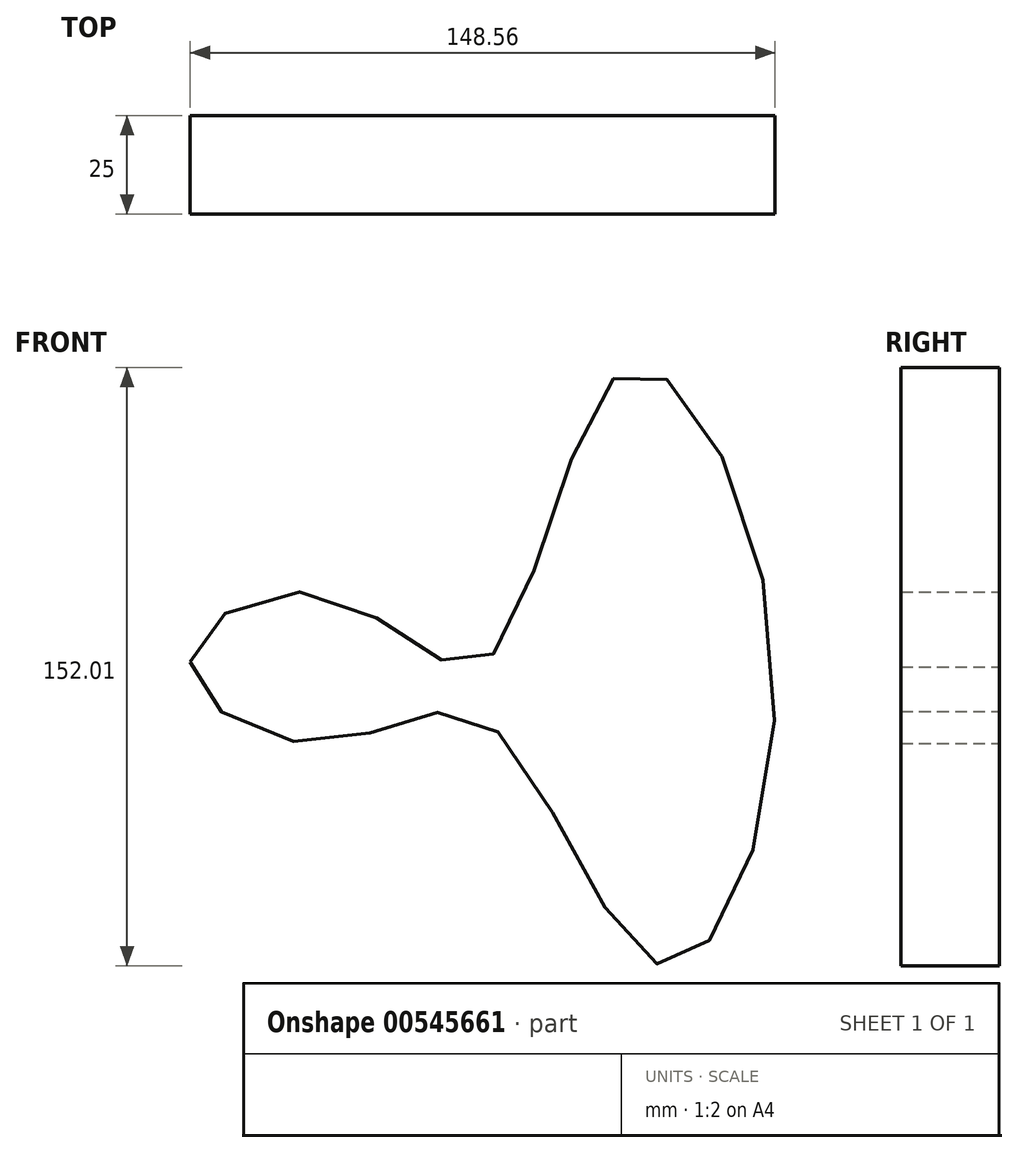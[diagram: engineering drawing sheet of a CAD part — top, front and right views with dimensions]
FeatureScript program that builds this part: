
annotation { "Feature Type Name" : "Feature", "Feature Type Description" : "" }
export const myFeature = defineFeature(function(context is Context, id is Id, definition is map)
    precondition{}
    {
        {
            var Q0;
            Q0=qCreatedBy(makeId("Front.planeOp"),FACE);
            var sketch = newSketch(context, id + "F0", { "sketchPlane" : qUnion([Q0])});
            skFitSpline(sketch, "E0", {"points": [v(-74.6, 0) * mm, v(-40.37, 17.11) * mm, v(0, 0) * mm, v(35.1, 73.72) * mm, v(73.72, 0) * mm, v(44.32, -76.8) * mm, v(0, -14.92) * mm, v(-41.69, -20.62) * mm, v(-74.6, 0) * mm]});
            skSolve(sketch);
        }
        {
            var Q0;
            Q0=makeQuery(id+"F0.imprint","IMPRINT",FACE,{"disambiguationData":[TD([[makeQuery(id+"F0.imprint","IMPRINT",EDGE,{"derivedFrom":sQuery(id+"F0.wireOp",EDGE,"E0")}),-1.0]])]});
            extrude(context, id + "F1", {"entities" : qUnion([Q0]), "depth" : 25 * mm, "offsetDistance" : 25 * mm});
        }
    });
